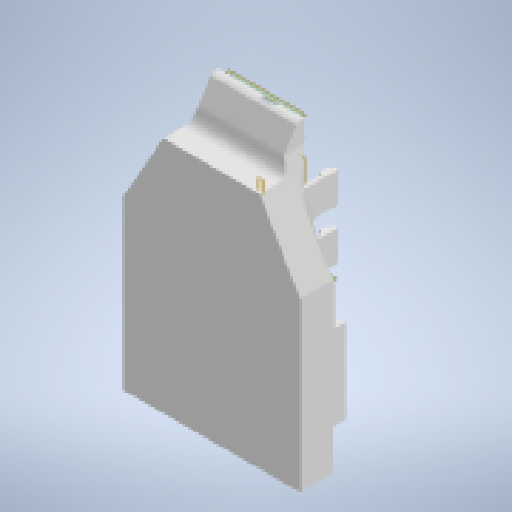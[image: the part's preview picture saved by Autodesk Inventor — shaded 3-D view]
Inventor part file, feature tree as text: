
AUTODESK INVENTOR PART (.ipt)
format: ipt  version: 2023.4 (Build 274418000, 418)  size: 791,040 bytes
history: native  units: mm
features: reference x27, extrude x16, other x10, plane x8, fillet x6, loft x5, sketch x2, chamfer x1
ambient origin geometry x8: Origin, YZ Plane, XZ Plane, XY Plane, X Axis, Y Axis, Z Axis, Center Point
bodies: Body1 (feature_tree)
feature tree (75):
  plane  "Work Plane2"
  extrude  "Extrusion2"  Depth=16.5mm
  extrude  "Extrusion5"  Depth=0.5mm
  plane  "Work Plane6"
  loft  "Loft2"
  extrude  "Extrusion6"  Depth=0.5mm TaperAngle=0.0deg
  extrude  "Extrusion7"  Depth=0.5mm
  plane  "Work Plane7"
  extrude  "Extrusion8"  Depth=0.5mm
  plane  "Work Plane8"
  extrude  "Extrusion11"  Depth=0.5mm
  plane  "Work Plane9"
  plane  "Work Plane10"
  plane  "Work Plane13"
  plane  "Work Plane11"
  extrude  "Extrusion13"  Depth=0.5mm
  extrude  "Extrusion14"  Depth=0.5mm
  extrude  "Extrusion16"  Depth=0.5mm TaperAngle=0.0deg
  extrude  "Extrusion17"  TaperAngle=0.0deg  [1 undecoded]
  extrude  "Extrusion18"  Depth=0.5mm
  loft  "Loft5"
  loft  "Loft6"
  loft  "Loft7"
  loft  "Loft8"
  extrude  "Extrusion19"  Depth=0.5mm TaperAngle=0.0deg
  fillet  "Fillet5"  Radius=0.5mm
  extrude  "Extrusion20"  Depth=0.5mm
  fillet  "Fillet7"  [1 undecoded]
  extrude  "Extrusion21"  TaperAngle=0.0deg  [1 undecoded]
  chamfer  "Chamfer3"  [1 undecoded]
  fillet  "Fillet8"  Radius=10.0mm
  fillet  "Fillet9"  Radius=2.0mm
  extrude  "Extrusion22"  Depth=0.5mm
  fillet  "Fillet10"  Radius=0.8mm
  fillet  "Fillet11"  Radius=10.0mm
  extrude  "Extrusion23"  Depth=0.5mm TaperAngle=0.0deg
  reference  "Reference1"
  reference  "Reference2"
  reference  "Reference3"
  reference  "Reference10"
  reference  "Reference11"
  reference  "Reference18"
  reference  "Reference19"
  reference  "Reference20"
  reference  "Reference22"
  reference  "Reference23"
  reference  "Reference24"
  reference  "Reference25"
  reference  "Reference26"
  reference  "Reference27"
  reference  "Reference28"
  reference  "Reference29"
  reference  "Reference30"
  other  "Edges1"
  reference  "Reference31"
  reference  "Reference32"
  reference  "Reference33"
  reference  "Reference34"
  reference  "Reference35"
  reference  "Reference36"
  reference  "Reference37"
  reference  "Reference41"
  reference  "Reference42"
  reference  "Reference43"
  sketch  "Sketch24"  dims[d0=17.5mm d1=16.5mm]
  other  "Edges4"
  other  "Edges5"
  other  "Edges6"
  sketch  "Sketch34"  dims[d2=8.0mm d3=9.5mm d4=7.0mm d7=0.4mm d8=0.0mm d29=0.4mm d30=0.4mm d31=0.4mm d32=0.4mm d33=0.4mm d34=2.8mm d35=0.0mm d36=0.0mm d37=90.0deg d40=0.4mm d42=0.4mm d43=3.988mm d44=0.0mm d46=0.2mm d47=0.2mm d48=2.75mm d49=0.0mm d55=0.5mm d56=-1.745329mm d63=0.4mm d64=0.0mm d65=90.0deg d73=0.0mm d74=0.0mm d78=10.0mm d79=0.0mm d80=2.0mm d81=0.4mm d82=0.8mm d95=10.0mm d96=0.0mm d97=8.3mm d98=0.0mm d102=10.0mm d103=0.0mm d104=0.3mm d105=0.6mm d106=0.3mm d107=0.0mm d109=0.3mm d110=0.6mm d111=0.3mm d112=0.0mm d113=0.4mm d114=0.0mm d115=90.0deg d116=0.0mm d117=90.0deg d118=2.0mm d119=0.4mm d120=0.0mm d121=90.0deg d122=0.0mm d123=90.0deg d124=0.4mm d125=2.0mm d126=0.0mm d127=90.0deg d128=0.0mm d129=90.0deg d130=0.0mm d131=90.0deg d132=0.0mm d133=90.0deg d136=0.2mm d137=0.0mm d138=1.0mm d143=0.22mm d144=0.22mm d145=10.0mm d146=0.0mm d147=2.0mm d148=0.1mm d149=0.1mm d150=0.0mm d152=1.0mm d153=0.1mm d154=0.1mm d155=0.5mm d156=-1.745329mm d157=0.2mm d158=2.0mm d159=45.0deg d160=1.0mm d162=1.2mm d163=6.0mm d164=0.6mm d165=0.3mm d166=0.0mm d168=0.5mm d169=0.1mm d170=6.0mm d171=6.0mm d172=2.5mm d173=2.5mm d174=0.5mm d175=0.6mm d176=1.5mm d178=0.5mm d179=2.8mm d180=0.0mm d181=2.5mm d94=0.0mm]
  parser-record x2  (decoder bookkeeping rows leaked as tree rows — omitted from the tree; the rows remain in map.json)
  other  "np1_full_assembly.iam"
  other  "np1_main_chassis:1"
  other  "full_assembly.iam"
  other  "probe_holder:1"
note: 4 required parameter values undecoded (feature->parameter linkage not recoverable at this tier; creation-order binding heuristic only, values carry confidence <= 0.55)
note: 2 file-system paths scrubbed to <path> (originals preserved in map.json)
